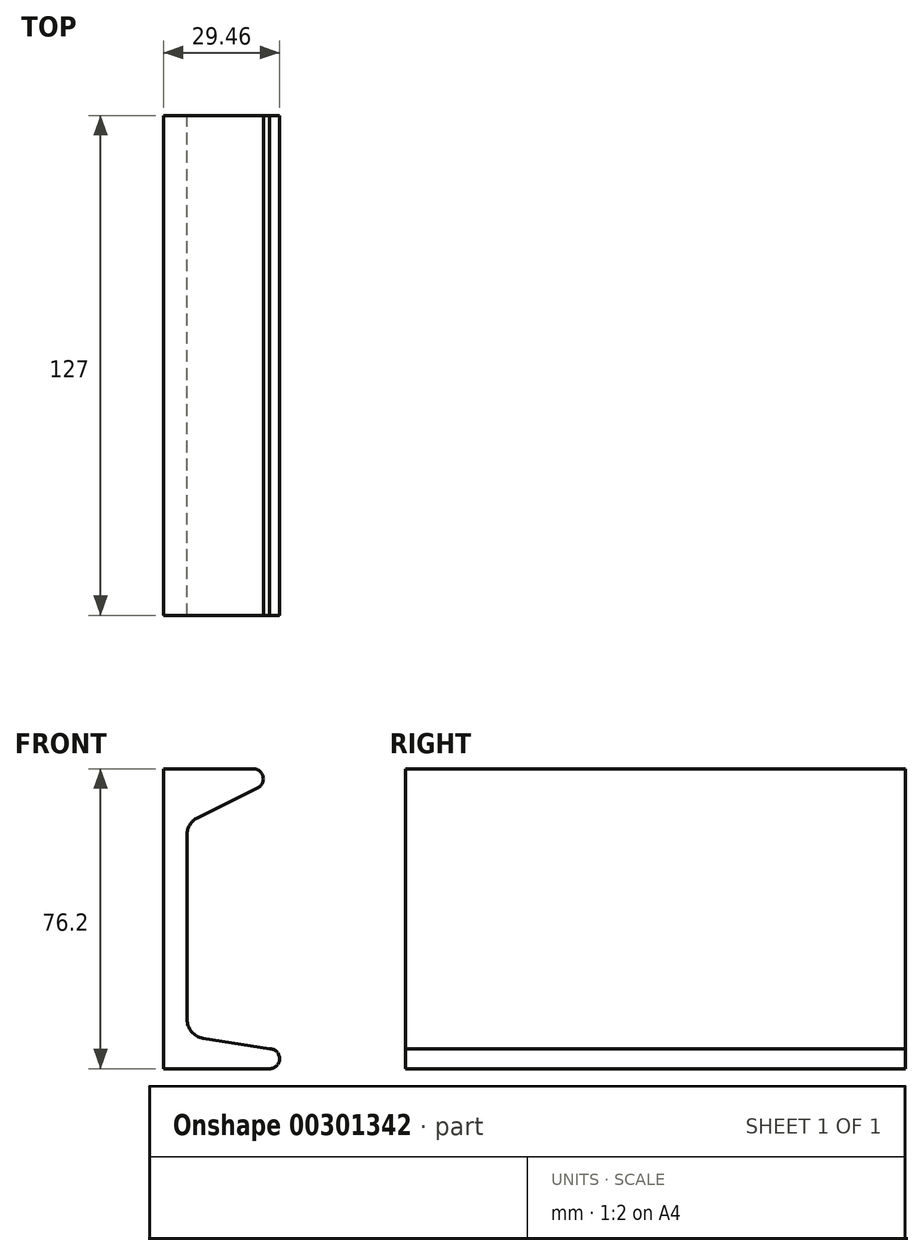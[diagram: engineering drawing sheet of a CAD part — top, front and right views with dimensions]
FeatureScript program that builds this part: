
annotation { "Feature Type Name" : "Feature", "Feature Type Description" : "" }
export const myFeature = defineFeature(function(context is Context, id is Id, definition is map)
    precondition{}
    {
        {
            var Q0;
            Q0=qCreatedBy(makeId("Front.planeOp"),FACE);
            var sketch = newSketch(context, id + "F0", { "sketchPlane" : qUnion([Q0])});
            skLineSegment(sketch, "E0", {"start": v(0, 76.2) * mm, "end": v(0, 0) * mm});
            skLineSegment(sketch, "E1", {"start": v(0, 0) * mm, "end": v(26.92, 0) * mm});
            skLineSegment(sketch, "E2", {"start": v(22.8, 76.2) * mm, "end": v(0, 76.2) * mm});
            skLineSegment(sketch, "E3", {"start": v(5.95, 59.42) * mm, "end": v(5.95, 12.55) * mm});
            skLineSegment(sketch, "E4", {"start": v(10.04, 7.75) * mm, "end": v(26.92, 5.08) * mm});
            skLineSegment(sketch, "E5", {"start": v(8.63, 63.76) * mm, "end": v(23.93, 71.39) * mm});
            skArc(sketch, "E6", {"start": v(23.93, 71.39) * mm, "mid": v(25.27, 74.24) * mm, "end": v(22.8, 76.2) * mm});
            skArc(sketch, "E7", {"start": v(26.92, 0) * mm, "mid": v(29.46, 2.54) * mm, "end": v(26.92, 5.08) * mm});
            skPoint(sketch, "E8.visualSharp", {"position": v(5.95, 62.42) * mm});
            skArc(sketch, "E8.filletArc", {"start": v(8.63, 63.76) * mm, "mid": v(6.67, 61.97) * mm, "end": v(5.95, 59.42) * mm});
            skPoint(sketch, "E9.visualSharp", {"position": v(5.95, 8.4) * mm});
            skArc(sketch, "E9.filletArc", {"start": v(5.95, 12.55) * mm, "mid": v(7.11, 9.4) * mm, "end": v(10.04, 7.75) * mm});
            skSolve(sketch);
        }
        {
            var Q0;
            Q0=makeQuery(id+"F0.imprint","IMPRINT",FACE,{"disambiguationData":[TD([[makeQuery(id+"F0.imprint","IMPRINT",EDGE,{"derivedFrom":sQuery(id+"F0.wireOp",EDGE,"E0")}),1.0]])]});
            var Q1;
            Q1=sQuery(id+"F0.wireOp",EDGE,"E2");
            extrude(context, id + "F1", {"entities" : qUnion([Q0]), "surfaceEntities" : qUnion([Q1]), "depth" : 127 * mm});
        }
    });
